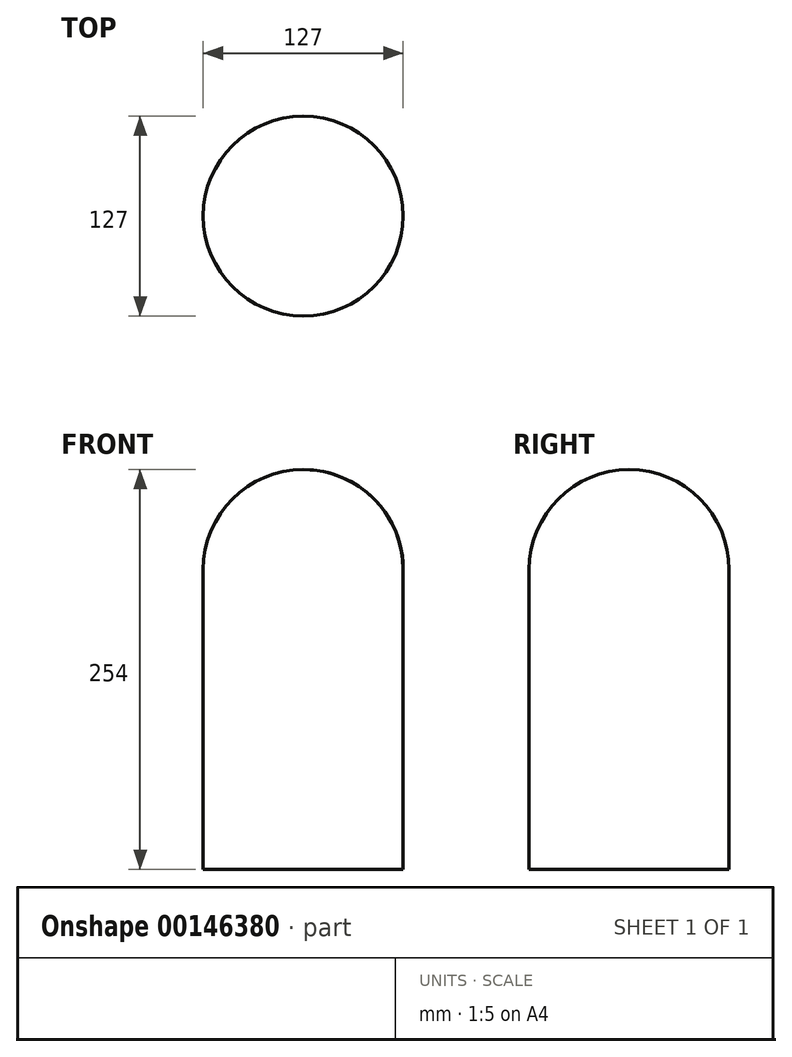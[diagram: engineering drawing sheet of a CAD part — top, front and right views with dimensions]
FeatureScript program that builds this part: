
annotation { "Feature Type Name" : "Feature", "Feature Type Description" : "" }
export const myFeature = defineFeature(function(context is Context, id is Id, definition is map)
    precondition{}
    {
        {
            var Q0;
            Q0=qCreatedBy(makeId("Top.planeOp"),FACE);
            var sketch = newSketch(context, id + "F0", { "sketchPlane" : qUnion([Q0])});
            skCircle(sketch, "E0", {"center": v(0, 0) * mm, "radius": 63.5 * mm});
            skCircle(sketch, "E1", {"center": v(0, 0) * mm, "radius": 57.15 * mm});
            skCircle(sketch, "E2", {"center": v(0, 0) * mm, "radius": 47.63 * mm});
            skSolve(sketch);
        }
        {
            var Q0;
            Q0=makeQuery(id+"F0.imprint","IMPRINT",FACE,{"disambiguationData":[TD([[makeQuery(id+"F0.imprint","IMPRINT",EDGE,{"derivedFrom":sQuery(id+"F0.wireOp",EDGE,"E0")}),1.0]])]});
            var Q1;
            Q1=makeQuery(id+"F0.imprint","IMPRINT",FACE,{"disambiguationData":[TD([[makeQuery(id+"F0.imprint","IMPRINT",EDGE,{"derivedFrom":sQuery(id+"F0.wireOp",EDGE,"E1")}),1.0]])]});
            var Q2;
            Q2=makeQuery(id+"F0.imprint","IMPRINT",FACE,{"disambiguationData":[TD([[makeQuery(id+"F0.imprint","IMPRINT",EDGE,{"derivedFrom":sQuery(id+"F0.wireOp",EDGE,"E2")}),1.0]])]});
            extrude(context, id + "F1", {"entities" : qUnion([Q0, Q1, Q2]), "depth" : 254 * mm});
        }
        {
            var Q0;
            Q0=makeQuery(id+"F1.opExtrude","CAP_EDGE",EDGE,{"disambiguationData":[OSD([sQuery(id+"F0.wireOp",EDGE,"E0")])],"isStart":false});
            fillet(context, id + "F2", {"entities" : qUnion([Q0]), "radius" : 63.5 * mm, "tangentPropagation" : true, "allowEdgeOverflow" : false});
        }
    });
